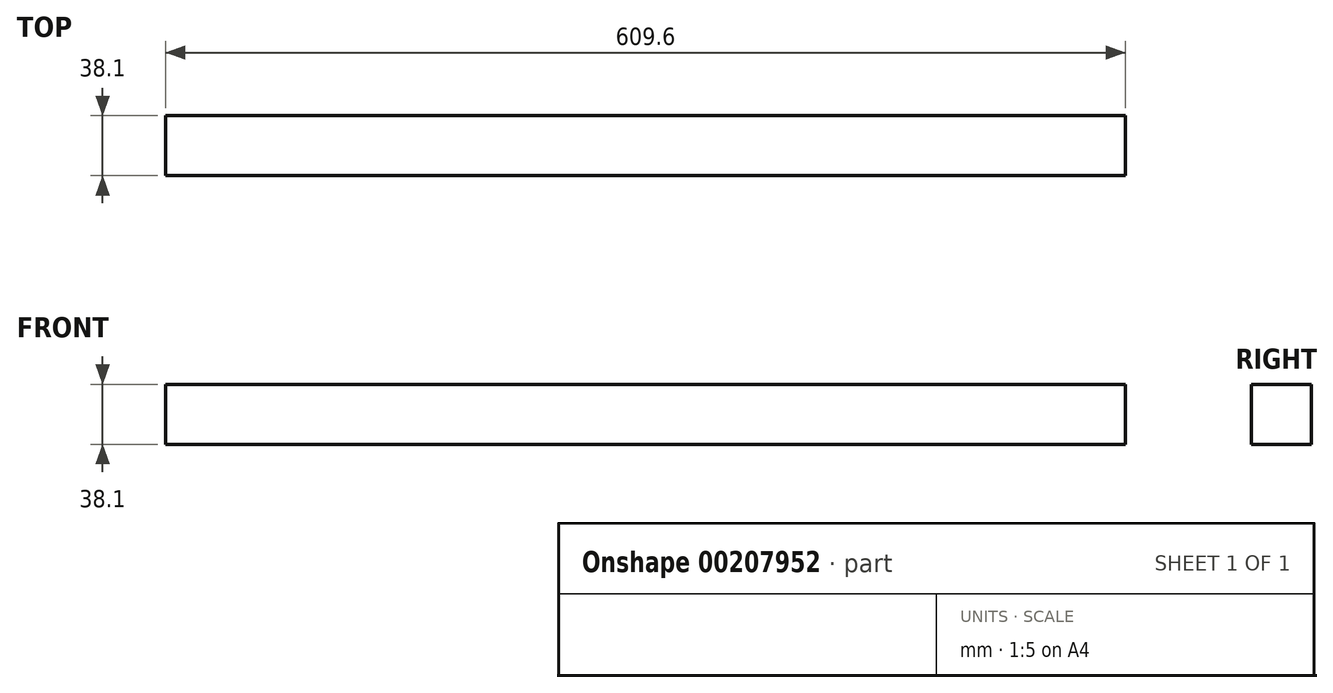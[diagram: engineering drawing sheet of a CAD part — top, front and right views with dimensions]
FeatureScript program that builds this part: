
annotation { "Feature Type Name" : "Feature", "Feature Type Description" : "" }
export const myFeature = defineFeature(function(context is Context, id is Id, definition is map)
    precondition{}
    {
        {
            var Q0;
            Q0=qCreatedBy(makeId("Right.planeOp"),FACE);
            var sketch = newSketch(context, id + "F0", { "sketchPlane" : qUnion([Q0])});
            skLineSegment(sketch, "E0.bottom", {"start": v(0, 0) * mm, "end": v(38.1, 0) * mm});
            skLineSegment(sketch, "E0.top", {"start": v(0, 38.1) * mm, "end": v(38.1, 38.1) * mm});
            skLineSegment(sketch, "E0.left", {"start": v(0, 0) * mm, "end": v(0, 38.1) * mm});
            skLineSegment(sketch, "E0.right", {"start": v(38.1, 0) * mm, "end": v(38.1, 38.1) * mm});
            skSolve(sketch);
        }
        {
            var Q0;
            Q0 = qSketchRegion(id + "F0", true);
            extrude(context, id + "F1", {"entities" : qUnion([Q0]), "depth" : 609.6 * mm});
        }
    });
